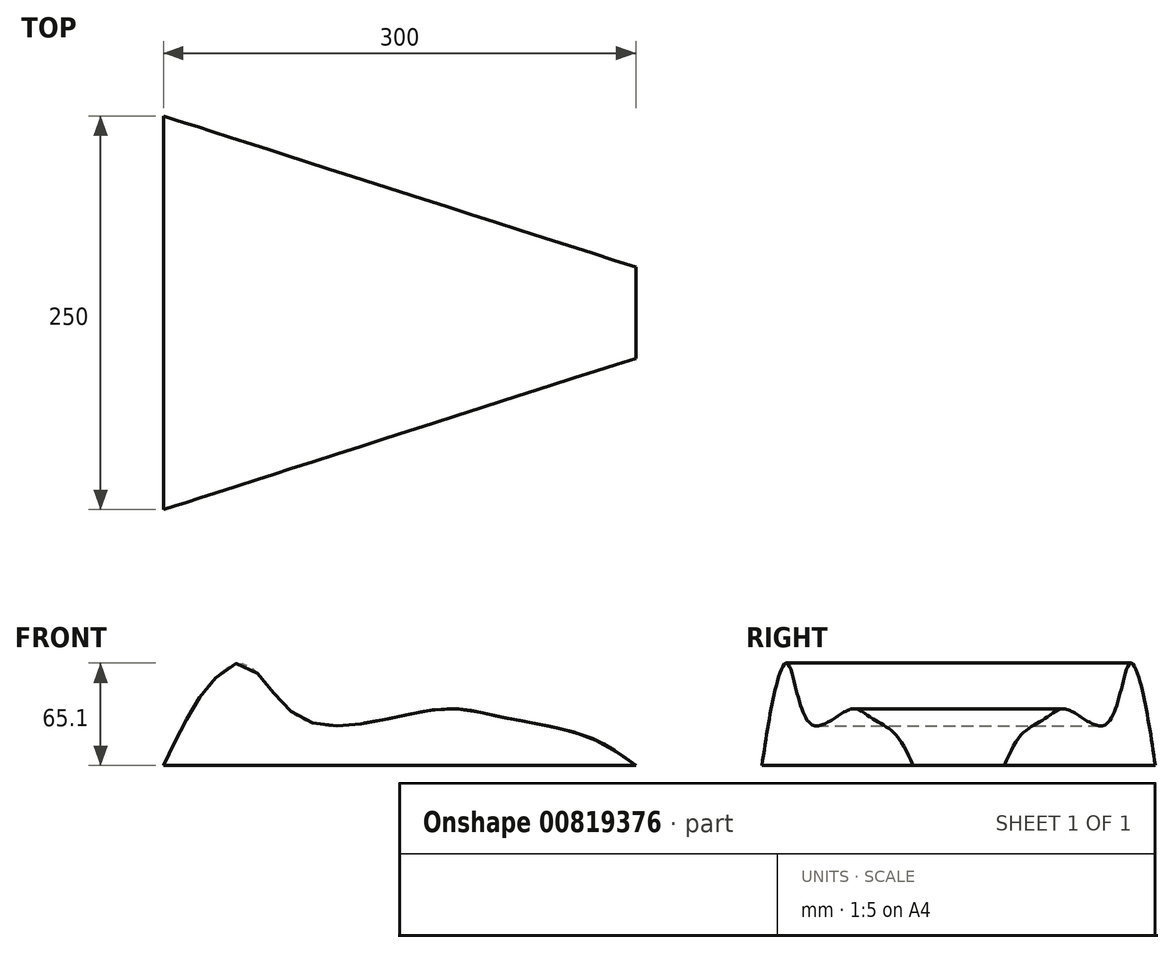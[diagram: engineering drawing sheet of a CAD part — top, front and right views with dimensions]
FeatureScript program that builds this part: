
annotation { "Feature Type Name" : "Feature", "Feature Type Description" : "" }
export const myFeature = defineFeature(function(context is Context, id is Id, definition is map)
    precondition{}
    {
        {
            var Q0;
            Q0=qCreatedBy(makeId("Front.planeOp"),FACE);
            var sketch = newSketch(context, id + "F0", { "sketchPlane" : qUnion([Q0])});
            skFitSpline(sketch, "E0", {"points": [v(-151.71, 0) * mm, v(-128.22, 44.05) * mm, v(-103.75, 65.09) * mm, v(-87.11, 52.85) * mm, v(-54.81, 26.43) * mm, v(23.5, 35.73) * mm, v(62.64, 30.83) * mm, v(116.97, 18.6) * mm, v(148.29, 0) * mm], "startDerivative": vector(160.86, 326.45) * mm, "endDerivative": vector(242.26, -172.77) * mm});
            skLineSegment(sketch, "E1", {"start": v(-151.71, 0) * mm, "end": v(148.29, 0) * mm});
            skSolve(sketch);
        }
        {
            var Q0;
            Q0=makeQuery(id+"F0.imprint","IMPRINT",FACE,{"disambiguationData":[TD([[makeQuery(id+"F0.imprint","IMPRINT",EDGE,{"derivedFrom":sQuery(id+"F0.wireOp",EDGE,"E0")}),-1.0]])]});
            extrude(context, id + "F1", {"entities" : qUnion([Q0]), "endBound" : BoundingType.SYMMETRIC, "depth" : 250 * mm, "offsetDistance" : 25 * mm});
        }
        {
            var Q0;
            Q0=makeQuery(id+"F1.opExtrude","SWEPT_FACE",FACE,{"disambiguationData":[OSD([sQuery(id+"F0.wireOp",EDGE,"E1")])]});
            var sketch = newSketch(context, id + "F2", { "sketchPlane" : qUnion([Q0])});
            skLineSegment(sketch, "E2", {"start": v(-151.71, 125) * mm, "end": v(148.29, 28.95) * mm});
            skLineSegment(sketch, "E3", {"start": v(148.29, 28.95) * mm, "end": v(148.29, -28.95) * mm});
            skLineSegment(sketch, "E4", {"start": v(148.29, -28.95) * mm, "end": v(-151.71, -125) * mm});
            skLineSegment(sketch, "E5", {"start": v(-151.71, 125) * mm, "end": v(237.6, 125) * mm});
            skLineSegment(sketch, "E6", {"start": v(237.6, 125) * mm, "end": v(237.6, -126.95) * mm});
            skLineSegment(sketch, "E7", {"start": v(237.6, -126.95) * mm, "end": v(-151.71, -125) * mm});
            skSolve(sketch);
        }
        {
            var Q0;
            {var subQ6=sQuery(id+"F2.wireOp",EDGE,"E3");Q0=makeQuery(id+"F2.imprint","IMPRINT",FACE,{"disambiguationData":[TD([[makeQuery(id+"F2.imprint","IMPRINT",EDGE,{"derivedFrom":subQ6}),1.0]])]});}
            var Q1;
            {var subQ0=sQuery(id+"F2.wireOp",EDGE,"E4");Q1=makeQuery(id+"F2.imprint","IMPRINT",FACE,{"disambiguationData":[TD([[makeQuery(id+"F2.imprint","IMPRINT",EDGE,{"derivedFrom":subQ0}),1.0]])]});}
            var Q2;
            {var subQ0=sQuery(id+"F2.wireOp",EDGE,"E2");Q2=makeQuery(id+"F2.imprint","IMPRINT",FACE,{"disambiguationData":[TD([[makeQuery(id+"F2.imprint","IMPRINT",EDGE,{"derivedFrom":subQ0}),1.0]])]});}
            extrude(context, id + "F3", {"entities" : qUnion([Q0, Q1, Q2]), "operationType" : NewBodyOperationType.REMOVE, "oppositeDirection" : true, "depth" : 100 * mm, "offsetDistance" : 25 * mm});
        }
    });
